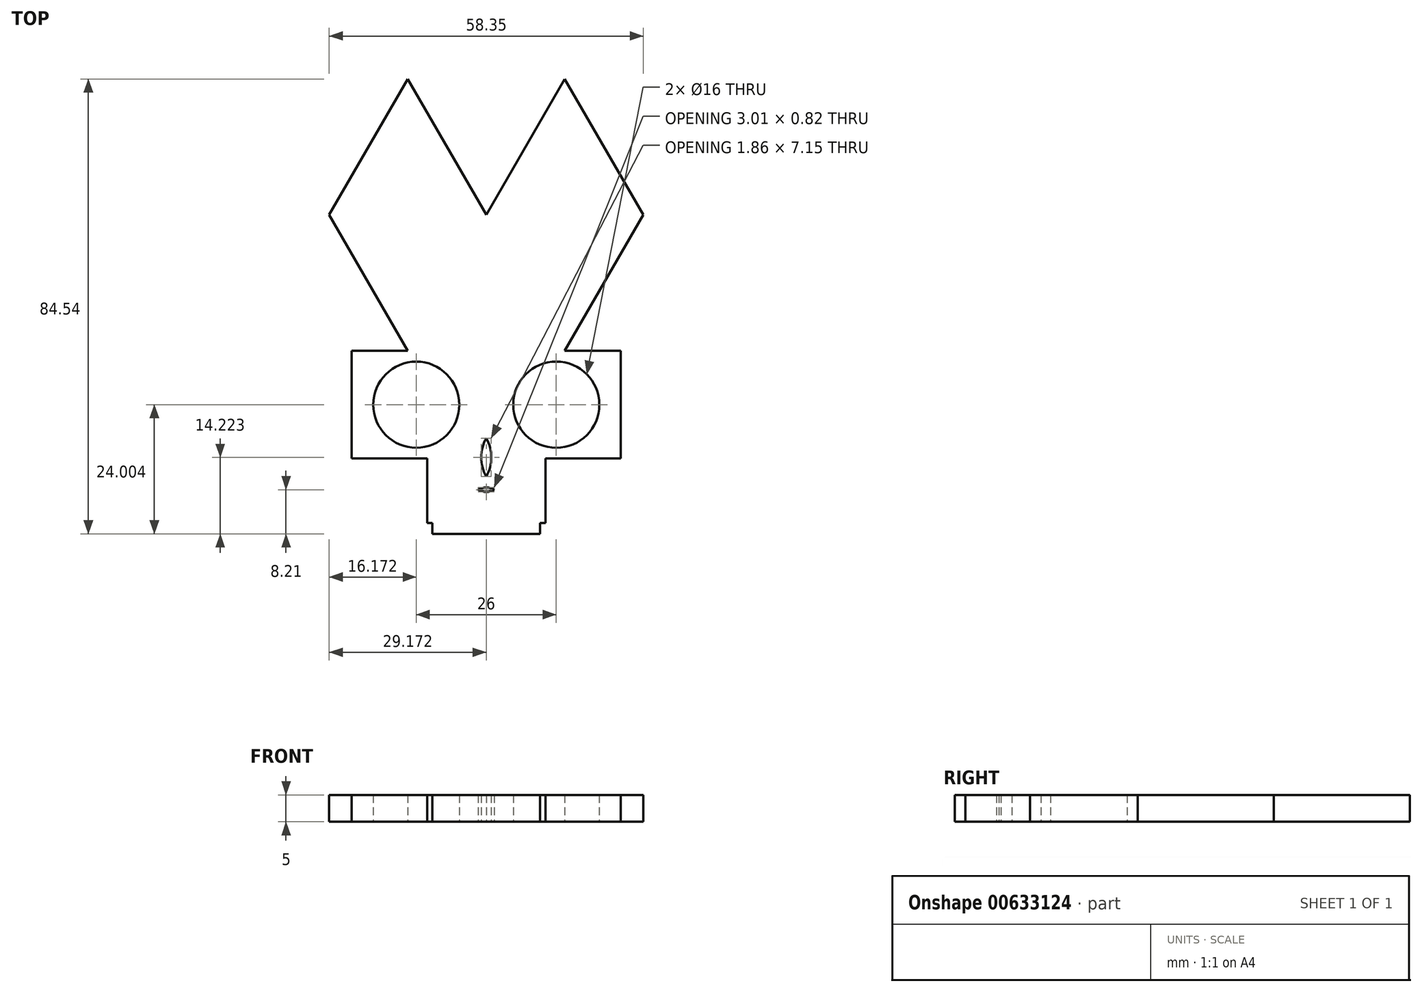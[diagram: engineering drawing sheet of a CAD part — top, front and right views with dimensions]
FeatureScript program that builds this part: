
annotation { "Feature Type Name" : "Feature", "Feature Type Description" : "" }
export const myFeature = defineFeature(function(context is Context, id is Id, definition is map)
    precondition{}
    {
        {
            var Q0;
            Q0=qCreatedBy(makeId("Top.planeOp"),FACE);
            var sketch = newSketch(context, id + "F0", { "sketchPlane" : qUnion([Q0])});
            skLineSegment(sketch, "E0.bottom", {"start": v(17.81, -25.27) * mm, "end": v(67.81, -25.27) * mm});
            skLineSegment(sketch, "E0.left", {"start": v(17.81, -25.27) * mm, "end": v(17.81, -45.27) * mm});
            skLineSegment(sketch, "E0.right", {"start": v(67.81, -25.27) * mm, "end": v(67.81, -45.27) * mm});
            skLineSegment(sketch, "E1", {"start": v(17.81, -45.27) * mm, "end": v(31.81, -45.27) * mm});
            skLineSegment(sketch, "E2.0", {"start": v(57.4, -25.27) * mm, "end": v(28.22, -25.27) * mm});
            skLineSegment(sketch, "E2.1", {"start": v(28.22, -25.27) * mm, "end": v(13.64, 0) * mm});
            skLineSegment(sketch, "E2.2", {"start": v(13.64, 0) * mm, "end": v(28.22, 25.27) * mm});
            skLineSegment(sketch, "E2.4", {"start": v(57.4, 25.27) * mm, "end": v(71.99, 0) * mm});
            skLineSegment(sketch, "E2.5", {"start": v(71.99, 0) * mm, "end": v(57.4, -25.27) * mm});
            skLineSegment(sketch, "E3", {"start": v(42.81, 0) * mm, "end": v(57.4, 25.27) * mm});
            skLineSegment(sketch, "E4", {"start": v(28.22, 25.27) * mm, "end": v(42.81, 0) * mm});
            skLineSegment(sketch, "E5.top", {"start": v(31.81, -57.27) * mm, "end": v(53.81, -57.27) * mm});
            skLineSegment(sketch, "E5.left", {"start": v(31.81, -45.27) * mm, "end": v(31.81, -57.27) * mm});
            skLineSegment(sketch, "E5.right", {"start": v(53.81, -45.27) * mm, "end": v(53.81, -57.27) * mm});
            skLineSegment(sketch, "E6", {"start": v(31.81, -57.27) * mm, "end": v(32.81, -57.27) * mm});
            skLineSegment(sketch, "E7.bottom", {"start": v(32.81, -57.27) * mm, "end": v(52.81, -57.27) * mm});
            skLineSegment(sketch, "E7.top", {"start": v(32.81, -59.27) * mm, "end": v(52.81, -59.27) * mm});
            skLineSegment(sketch, "E7.left", {"start": v(32.81, -57.27) * mm, "end": v(32.81, -59.27) * mm});
            skLineSegment(sketch, "E7.right", {"start": v(52.81, -57.27) * mm, "end": v(52.81, -59.27) * mm});
            skLineSegment(sketch, "E8.bottom", {"start": v(17.81, -25.27) * mm, "end": v(17.81, -25.27) * mm});
            skLineSegment(sketch, "E8.top", {"start": v(17.81, -35.27) * mm, "end": v(17.81, -35.27) * mm});
            skLineSegment(sketch, "E8.left", {"start": v(17.81, -25.27) * mm, "end": v(17.81, -35.27) * mm});
            skLineSegment(sketch, "E8.right", {"start": v(17.81, -25.27) * mm, "end": v(17.81, -35.27) * mm});
            skCircle(sketch, "E9", {"center": v(29.81, -35.27) * mm, "radius": 8 * mm});
            skCircle(sketch, "E10", {"center": v(55.81, -35.27) * mm, "radius": 8 * mm});
            skPoint(sketch, "E11.endSnap0", {"position": v(42.81, -45.27) * mm});
            skLineSegment(sketch, "E12", {"start": v(53.81, -45.27) * mm, "end": v(67.81, -45.27) * mm});
            skArc(sketch, "E13", {"start": v(42.81, -48.62) * mm, "mid": v(43.74, -45.05) * mm, "end": v(42.81, -41.47) * mm});
            skArc(sketch, "E14.MirrorCS", {"start": v(42.81, -48.62) * mm, "mid": v(41.88, -45.05) * mm, "end": v(42.81, -41.47) * mm});
            skArc(sketch, "E15", {"start": v(41.3, -51.06) * mm, "mid": v(42.81, -51.47) * mm, "end": v(44.32, -51.06) * mm});
            skArc(sketch, "E16.MirrorCS", {"start": v(41.3, -51.06) * mm, "mid": v(42.81, -50.65) * mm, "end": v(44.32, -51.06) * mm});
            skSolve(sketch);
        }
        {
            var Q0;
            Q0 = qSketchRegion(id + "F0", true);
            extrude(context, id + "F1", {"entities" : qUnion([Q0]), "depth" : 5 * mm, "offsetDistance" : 25 * mm});
        }
    });
